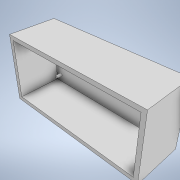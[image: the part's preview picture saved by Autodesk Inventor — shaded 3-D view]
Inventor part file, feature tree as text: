
AUTODESK INVENTOR PART (.ipt)
format: ipt  version: 2020.1 (Build 241239000, 239)  size: 117,248 bytes
history: native  units: mm
features: extrude x2, sketch x2, shell x1
ambient origin geometry x8: Origin, YZ Plane, XZ Plane, XY Plane, X Axis, Y Axis, Z Axis, Center Point
bodies: Solid1 (feature_tree)
feature tree (5):
  extrude  "Extrusion1"  Depth=32.0mm
  shell  "Shell1"  Thickness=23.0mm
  extrude  "Extrusion2"  Depth=5.0mm
  sketch  "Sketch1"  dims[d0=68.0mm d1=32.0mm d2=23.0mm d3=0.0mm]
  sketch  "Sketch5"  dims[d4=2.0mm d5=5.0mm d6=16.0mm d7=10.25mm d8=57.5mm d9=20.5mm d10=1.5mm d11=1.5mm d12=1.5mm d13=1.5mm d14=3.0mm d15=0.0mm]
